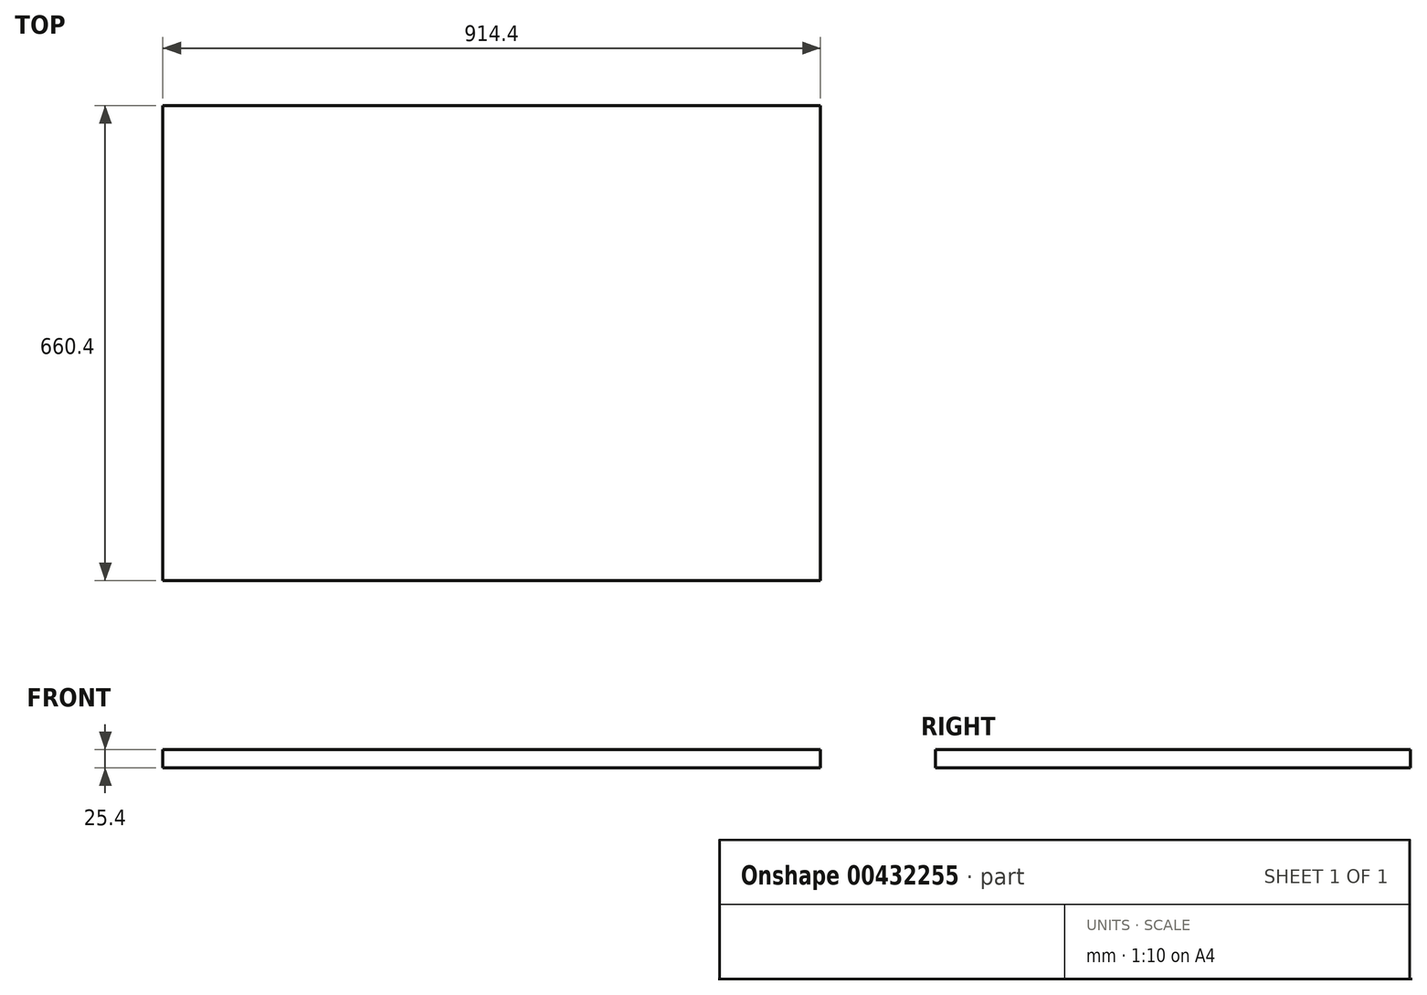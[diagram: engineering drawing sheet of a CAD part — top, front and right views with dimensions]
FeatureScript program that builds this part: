
annotation { "Feature Type Name" : "Feature", "Feature Type Description" : "" }
export const myFeature = defineFeature(function(context is Context, id is Id, definition is map)
    precondition{}
    {
        {
            var Q0;
            Q0=qCreatedBy(makeId("Top.planeOp"),FACE);
            var sketch = newSketch(context, id + "F0", { "sketchPlane" : qUnion([Q0])});
            skLineSegment(sketch, "E0.bottom", {"start": v(-457.2, -330.2) * mm, "end": v(457.2, -330.2) * mm});
            skLineSegment(sketch, "E0.top", {"start": v(-457.2, 330.2) * mm, "end": v(457.2, 330.2) * mm});
            skLineSegment(sketch, "E0.left", {"start": v(-457.2, -330.2) * mm, "end": v(-457.2, 330.2) * mm});
            skLineSegment(sketch, "E0.right", {"start": v(457.2, -330.2) * mm, "end": v(457.2, 330.2) * mm});
            skPoint(sketch, "E0.middle", {"position": v(0, 0) * mm});
            skSolve(sketch);
        }
        {
            var Q0;
            Q0 = qSketchRegion(id + "F0", true);
            extrude(context, id + "F1", {"entities" : qUnion([Q0]), "oppositeDirection" : true, "depth" : 25.4 * mm});
        }
    });
